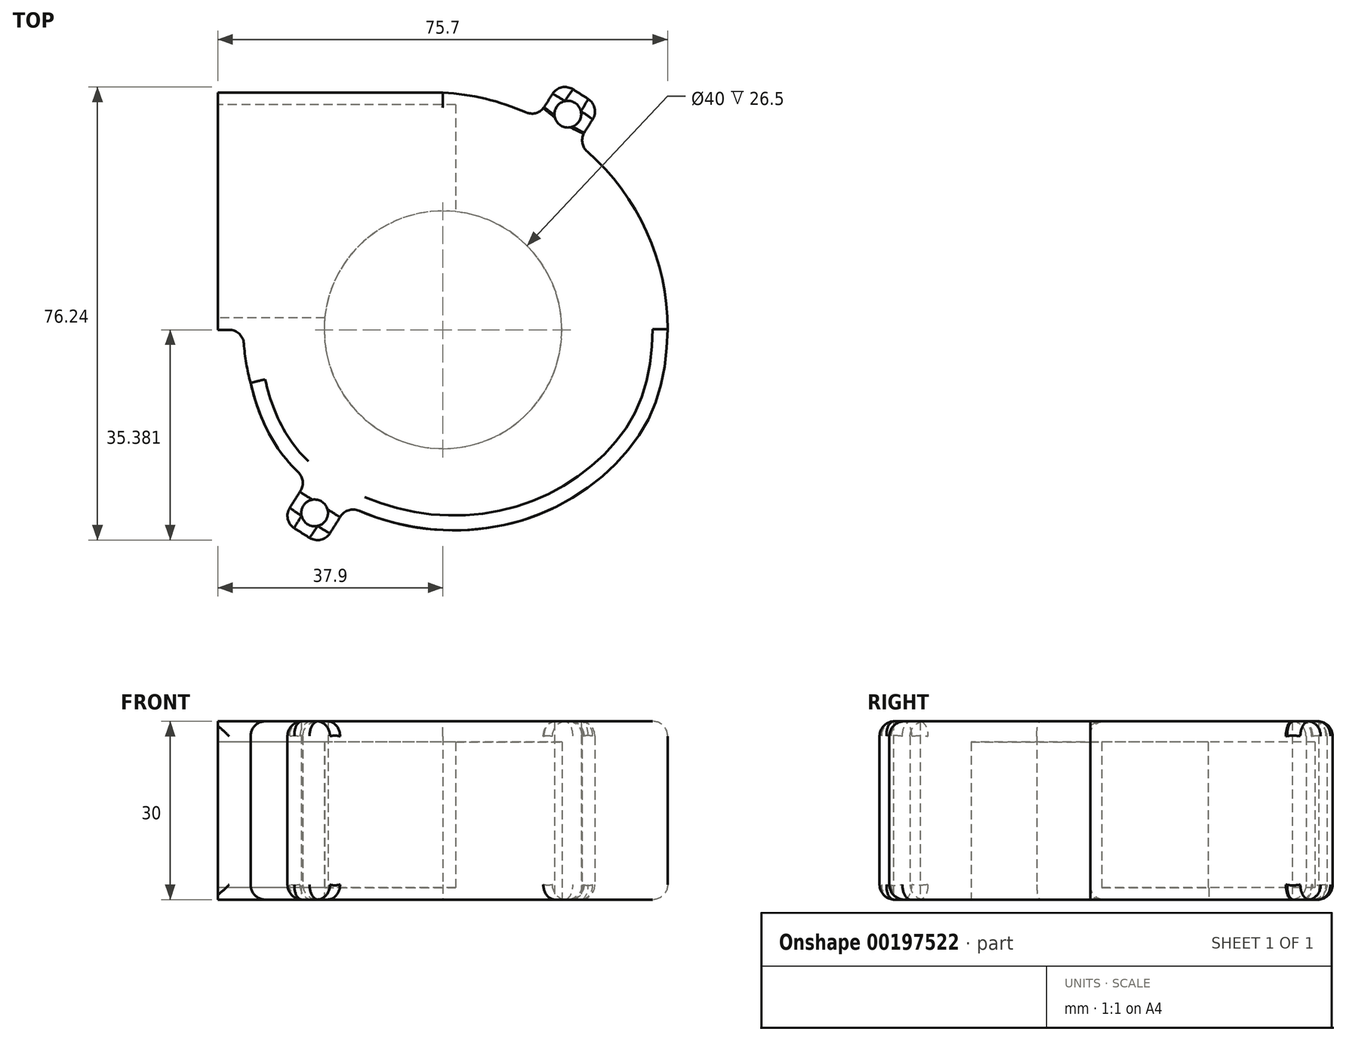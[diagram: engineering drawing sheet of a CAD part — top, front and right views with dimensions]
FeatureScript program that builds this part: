
annotation { "Feature Type Name" : "Feature", "Feature Type Description" : "" }
export const myFeature = defineFeature(function(context is Context, id is Id, definition is map)
    precondition{}
    {
        {
            var Q0;
            Q0=qCreatedBy(makeId("Top.planeOp"),FACE);
            var sketch = newSketch(context, id + "F0", { "sketchPlane" : qUnion([Q0])});
            skCircle(sketch, "E0", {"center": v(0, -0.09) * mm, "radius": 20 * mm, "construction": true});
            skCircle(sketch, "E1", {"center": v(21, 36.2) * mm, "radius": 2.25 * mm});
            skCircle(sketch, "E2", {"center": v(-21.6, -30.9) * mm, "radius": 2.25 * mm});
            skLineSegment(sketch, "E3.bottom", {"start": v(-37.9, 39.81) * mm, "end": v(0, 39.81) * mm});
            skLineSegment(sketch, "E3.top", {"start": v(-37.9, -0.09) * mm, "end": v(0, -0.09) * mm});
            skLineSegment(sketch, "E3.left", {"start": v(-37.9, 39.81) * mm, "end": v(-37.9, -0.09) * mm});
            skLineSegment(sketch, "E3.right", {"start": v(0, 19.91) * mm, "end": v(0, -0.09) * mm});
            skArc(sketch, "E4", {"start": v(-33.58, -0.09) * mm, "mid": v(-33.28, -4.6) * mm, "end": v(-32.37, -9.03) * mm});
            skFitSpline(sketch, "E5", {"points": [v(37.8, 0) * mm, v(30.81, -20.72) * mm, v(15.41, -31.43) * mm, v(-6.23, -33.01) * mm, v(-25.6, -22.76) * mm, v(-32.37, -9.03) * mm, v(-33.58, 0) * mm], "startDerivative": vector(-3.22, -160.72) * mm, "endDerivative": vector(-3.5, 61.67) * mm});
            skArc(sketch, "E6.trimOffspring", {"start": v(37.8, 0) * mm, "mid": v(33.8, 17.4) * mm, "end": v(22.63, 31.3) * mm});
            skLineSegment(sketch, "E7", {"start": v(21, 36.2) * mm, "end": v(-21.6, -30.9) * mm, "construction": true});
            skLineSegment(sketch, "E8", {"start": v(19.77, 41.72) * mm, "end": v(15.88, 35.6) * mm});
            skLineSegment(sketch, "E9", {"start": v(-27.12, -32.13) * mm, "end": v(-20.37, -36.42) * mm});
            skLineSegment(sketch, "E10", {"start": v(-20.37, -36.42) * mm, "end": v(-16.07, -29.66) * mm});
            skLineSegment(sketch, "E11", {"start": v(26.52, 37.43) * mm, "end": v(19.77, 41.72) * mm});
            skArc(sketch, "E12.trimOffspring", {"start": v(15.88, 35.6) * mm, "mid": v(8.16, 38.53) * mm, "end": v(0, 39.81) * mm});
            skLineSegment(sketch, "E13.trimOffspring", {"start": v(22.63, 31.3) * mm, "end": v(26.52, 37.43) * mm});
            skLineSegment(sketch, "E14.trimOffspring", {"start": v(-22.83, -25.37) * mm, "end": v(-27.12, -32.13) * mm});
            skSolve(sketch);
        }
        {
            var Q0;
            Q0=qSketchRegion(id+"F0",true);
            extrude(context, id + "F1", {"entities" : qUnion([Q0]), "depth" : 30 * mm});
        }
        {
            var Q0;
            Q0=makeQuery(id+"F1.opExtrude","SWEPT_EDGE",EDGE,{"disambiguationData":[OSD([sQuery(id+"F0.wireOp",EDGE,"E5"),sQuery(id+"F0.wireOp",EDGE,"E10")])]});
            var Q1;
            Q1=makeQuery(id+"F1.opExtrude","SWEPT_EDGE",EDGE,{"disambiguationData":[OSD([sQuery(id+"F0.wireOp",EDGE,"E9"),sQuery(id+"F0.wireOp",EDGE,"E10")])]});
            var Q2;
            Q2=makeQuery(id+"F1.opExtrude","SWEPT_EDGE",EDGE,{"disambiguationData":[OSD([sQuery(id+"F0.wireOp",EDGE,"E9"),sQuery(id+"F0.wireOp",EDGE,"E14.trimOffspring")])]});
            var Q3;
            Q3=makeQuery(id+"F1.opExtrude","SWEPT_EDGE",EDGE,{"disambiguationData":[OSD([sQuery(id+"F0.wireOp",EDGE,"E14.trimOffspring"),sQuery(id+"F0.wireOp",EDGE,"E5")])]});
            var Q4;
            Q4=makeQuery(id+"F1.opExtrude","SWEPT_EDGE",EDGE,{"disambiguationData":[OSD([sQuery(id+"F0.wireOp",EDGE,"E11"),sQuery(id+"F0.wireOp",EDGE,"E13.trimOffspring")])]});
            var Q5;
            Q5=makeQuery(id+"F1.opExtrude","SWEPT_EDGE",EDGE,{"disambiguationData":[OSD([sQuery(id+"F0.wireOp",EDGE,"E6.trimOffspring"),sQuery(id+"F0.wireOp",EDGE,"E13.trimOffspring")])]});
            var Q6;
            Q6=makeQuery(id+"F1.opExtrude","SWEPT_EDGE",EDGE,{"disambiguationData":[OSD([sQuery(id+"F0.wireOp",EDGE,"E8"),sQuery(id+"F0.wireOp",EDGE,"E11")])]});
            var Q7;
            Q7=makeQuery(id+"F1.opExtrude","SWEPT_EDGE",EDGE,{"disambiguationData":[OSD([sQuery(id+"F0.wireOp",EDGE,"E8"),sQuery(id+"F0.wireOp",EDGE,"E12.trimOffspring")])]});
            fillet(context, id + "F2", {"entities" : qUnion([Q0, Q1, Q2, Q3, Q4, Q5, Q6, Q7]), "radius" : 2.5 * mm, "tangentPropagation" : true, "allowEdgeOverflow" : false});
        }
        {
            var Q0;
            Q0=makeQuery(id+"F1.opExtrude","CAP_FACE",FACE,{"disambiguationData":[OSD([sQuery(id+"F0.wireOp",EDGE,"E1"),sQuery(id+"F0.wireOp",EDGE,"E2"),sQuery(id+"F0.wireOp",EDGE,"E3.bottom"),sQuery(id+"F0.wireOp",EDGE,"E3.top"),sQuery(id+"F0.wireOp",EDGE,"E3.left"),sQuery(id+"F0.wireOp",EDGE,"E4"),sQuery(id+"F0.wireOp",EDGE,"E5"),sQuery(id+"F0.wireOp",EDGE,"E6.trimOffspring"),sQuery(id+"F0.wireOp",EDGE,"E8"),sQuery(id+"F0.wireOp",EDGE,"E9"),sQuery(id+"F0.wireOp",EDGE,"E10"),sQuery(id+"F0.wireOp",EDGE,"E11"),sQuery(id+"F0.wireOp",EDGE,"E12.trimOffspring"),sQuery(id+"F0.wireOp",EDGE,"E13.trimOffspring"),sQuery(id+"F0.wireOp",EDGE,"E14.trimOffspring"),sQuery(id+"F0.wireOp",EDGE,"E5")])],"isStart":true});
            var sketch = newSketch(context, id + "F3", { "sketchPlane" : qUnion([Q0])});
            skCircle(sketch, "E15.0", {"center": v(0, 0.09) * mm, "radius": 20 * mm});
            skSolve(sketch);
        }
        {
            var Q0;
            Q0=qSketchRegion(id+"F3",true);
            extrude(context, id + "F4", {"entities" : qUnion([Q0]), "operationType" : NewBodyOperationType.REMOVE, "oppositeDirection" : true, "depth" : 26.5 * mm});
        }
        {
            var Q0;
            Q0=makeQuery(id+"F1.opExtrude","SWEPT_FACE",FACE,{"disambiguationData":[OSD([sQuery(id+"F0.wireOp",EDGE,"E3.left")])]});
            var sketch = newSketch(context, id + "F5", { "sketchPlane" : qUnion([Q0])});
            skLineSegment(sketch, "E16.bottom", {"start": v(-37.81, 26.5) * mm, "end": v(-1.91, 26.5) * mm});
            skLineSegment(sketch, "E16.top", {"start": v(-37.81, 2) * mm, "end": v(-1.91, 2) * mm});
            skLineSegment(sketch, "E16.left", {"start": v(-37.81, 26.5) * mm, "end": v(-37.81, 2) * mm});
            skLineSegment(sketch, "E16.right", {"start": v(-1.91, 26.5) * mm, "end": v(-1.91, 2) * mm});
            skSolve(sketch);
        }
        {
            var Q0;
            Q0=qSketchRegion(id+"F5",true);
            extrude(context, id + "F6", {"entities" : qUnion([Q0]), "operationType" : NewBodyOperationType.REMOVE, "oppositeDirection" : true, "depth" : 40 * mm});
        }
        {
            var Q0;
            Q0=makeQuery(id+"F1.opExtrude","SWEPT_EDGE",EDGE,{"disambiguationData":[OSD([sQuery(id+"F0.wireOp",EDGE,"E3.top"),sQuery(id+"F0.wireOp",EDGE,"E4")])]});
            var Q1;
            Q1=makeQuery(id+"F1.opExtrude","CAP_EDGE",EDGE,{"disambiguationData":[OSD([sQuery(id+"F0.wireOp",EDGE,"E3.bottom")])],"isStart":true});
            var Q2;
            Q2=makeQuery(id+"F1.opExtrude","CAP_EDGE",EDGE,{"disambiguationData":[OSD([sQuery(id+"F0.wireOp",EDGE,"E12.trimOffspring")])],"isStart":true});
            var Q3;
            Q3=makeQuery(id+"F4.boolean.opBoolean","COPY",EDGE,{"derivedFrom":makeQuery(id+"F4.opExtrude","CAP_EDGE",EDGE,{"disambiguationData":[OSD([sQuery(id+"F3.wireOp",EDGE,"E15.0")])],"isStart":true})});
            var Q4;
            Q4=makeQuery(id+"F1.opExtrude","CAP_EDGE",EDGE,{"disambiguationData":[OSD([sQuery(id+"F0.wireOp",EDGE,"E5")])],"isStart":true});
            var Q5;
            Q5=makeQuery(id+"F1.opExtrude","CAP_EDGE",EDGE,{"disambiguationData":[OSD([sQuery(id+"F0.wireOp",EDGE,"E3.bottom")])],"isStart":false});
            var Q6;
            Q6=makeQuery(id+"F1.opExtrude","CAP_EDGE",EDGE,{"disambiguationData":[OSD([sQuery(id+"F0.wireOp",EDGE,"E12.trimOffspring")])],"isStart":false});
            var Q7;
            Q7=makeQuery(id+"F1.opExtrude","CAP_EDGE",EDGE,{"disambiguationData":[OSD([sQuery(id+"F0.wireOp",EDGE,"E5")])],"isStart":false});
            fillet(context, id + "F7", {"entities" : qUnion([Q0, Q1, Q2, Q3, Q4, Q5, Q6, Q7]), "radius" : 2.5 * mm, "tangentPropagation" : true, "allowEdgeOverflow" : false});
        }
    });
